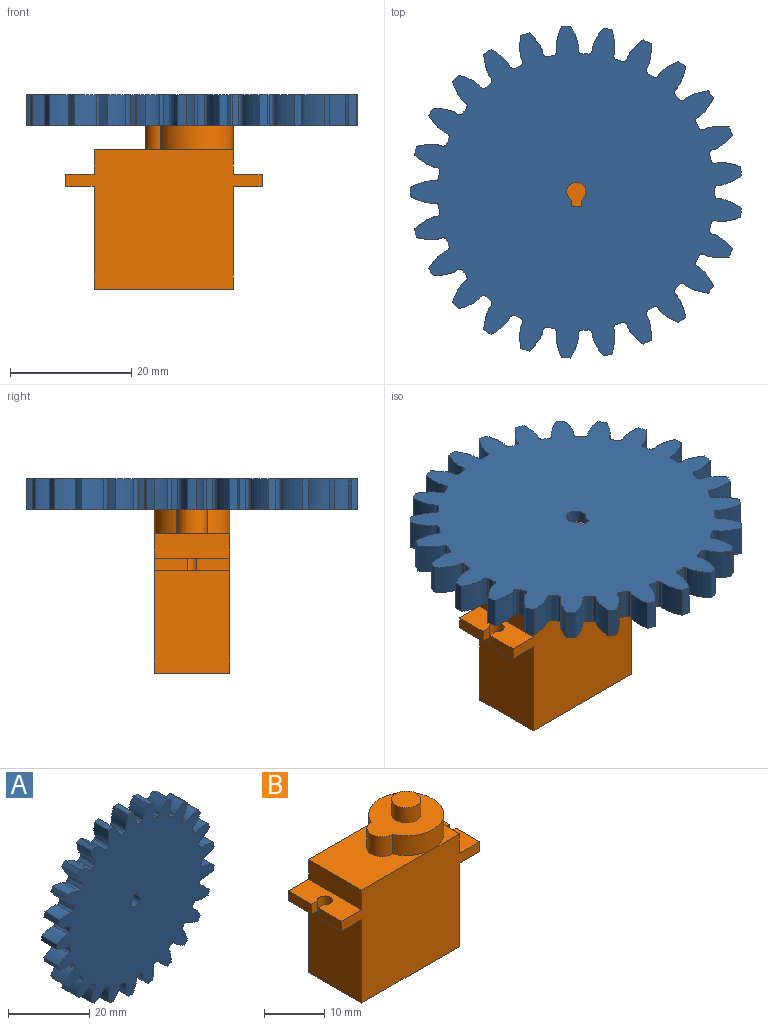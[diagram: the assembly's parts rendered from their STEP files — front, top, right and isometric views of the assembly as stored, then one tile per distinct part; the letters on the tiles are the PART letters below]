
ASSEMBLY  parts=2 mates=1
PART A: 156 faces, bbox 54.7x5.1x54.8 mm
  f0: cylinder r=27.43mm len=5.08mm, axis (0,1,0), area 7.4mm2, adj f24,f30,f141,f153
  f1: cylinder r=27.43mm len=5.08mm, axis (0,1,0), area 7.4mm2, adj f24,f30,f148,f151
  f2: cylinder r=27.43mm len=5.08mm, axis (0,1,0), area 7.4mm2, adj f24,f30,f136,f143
  f3: cylinder r=27.43mm len=5.08mm, axis (0,1,0), area 7.4mm2, adj f24,f30,f131,f138
  f4: cylinder r=27.43mm len=5.08mm, axis (0,1,0), area 7.4mm2, adj f24,f30,f126,f133
  f5: cylinder r=27.43mm len=5.08mm, axis (0,1,0), area 7.4mm2, adj f24,f30,f116,f128
  f6: cylinder r=27.43mm len=5.08mm, axis (0,1,0), area 7.4mm2, adj f24,f30,f111,f123
  f7: cylinder r=27.43mm len=5.08mm, axis (0,1,0), area 7.4mm2, adj f24,f30,f118,f121
  f8: cylinder r=27.43mm len=5.08mm, axis (0,1,0), area 7.4mm2, adj f24,f30,f106,f113
  f9: cylinder r=27.43mm len=5.08mm, axis (0,1,0), area 7.4mm2, adj f24,f30,f101,f108
  f10: cylinder r=27.43mm len=5.08mm, axis (0,1,0), area 7.4mm2, adj f24,f30,f96,f103
  f11: cylinder r=27.43mm len=5.08mm, axis (0,1,0), area 7.4mm2, adj f24,f30,f81,f98
  f12: cylinder r=27.43mm len=5.08mm, axis (0,1,0), area 7.4mm2, adj f24,f30,f31,f93
  f13: cylinder r=27.43mm len=5.08mm, axis (0,1,0), area 7.4mm2, adj f24,f30,f88,f91
  f14: cylinder r=27.43mm len=5.08mm, axis (0,1,0), area 7.4mm2, adj f24,f30,f76,f83
  f15: cylinder r=27.43mm len=5.08mm, axis (0,1,0), area 7.4mm2, adj f24,f30,f78,f86
  f16: cylinder r=27.43mm len=5.08mm, axis (0,1,0), area 7.4mm2, adj f24,f30,f73,f146
  f17: cylinder r=27.43mm len=5.08mm, axis (0,1,0), area 7.4mm2, adj f24,f30,f68,f71
  f18: cylinder r=27.43mm len=5.08mm, axis (0,1,0), area 7.4mm2, adj f24,f30,f63,f66
  f19: cylinder r=27.43mm len=5.08mm, axis (0,1,0), area 7.4mm2, adj f24,f30,f58,f61
  f20: cylinder r=27.43mm len=5.08mm, axis (0,1,0), area 7.4mm2, adj f24,f30,f46,f53
  f21: cylinder r=27.43mm len=5.08mm, axis (0,1,0), area 7.4mm2, adj f24,f30,f36,f48
  f22: cylinder r=27.43mm len=5.08mm, axis (0,1,0), area 7.4mm2, adj f24,f30,f43,f56
  f23: cylinder r=27.43mm len=5.08mm, axis (0,1,0), area 7.4mm2, adj f24,f30,f38,f41
  f24: plane 54.85x54.74mm, normal (0,-1,0), area 1985mm2, adj f0,f1,f2,f3,f4,f5,f6,f7
  f25: plane 5.08x1.01mm, normal (-1,0,0), area 5.1mm2, adj f24,f26,f28,f30
  f26: cylinder r=1.59mm len=5.08mm, axis (0,1,0), area 42.2mm2, adj f24,f25,f27,f30
  f27: plane 5.08x1.01mm, normal (1,0,0), area 5.1mm2, adj f24,f26,f28,f30
  f28: plane 5.08x1.59mm, normal (0,0,-1), area 8.1mm2, adj f24,f25,f27,f30
  f29: cylinder r=27.43mm len=5.08mm, axis (0,1,0), area 7.4mm2, adj f24,f30,f33,f51
  f30: plane 54.85x54.74mm, normal (0,1,0), area 1985mm2, adj f0,f1,f2,f3,f4,f5,f6,f7
  f31: extruded ~5.08x3.89mm, area 21.7mm2, adj f12,f24,f30,f34
  f32: cylinder r=22.86mm len=5.08mm, axis (0,1,0), area 5.4mm2, adj f24,f30,f34,f35
  f33: extruded ~5.08x3.89mm, area 21.7mm2, adj f24,f29,f30,f35
  f34: cylinder r=0.58mm len=5.08mm, axis (0,1,0), area 4.5mm2, adj f24,f30,f31,f32
  f35: cylinder r=0.58mm len=5.08mm, axis (0,1,0), area 4.5mm2, adj f24,f30,f32,f33
  f36: extruded ~5.08x3.93mm, area 21.7mm2, adj f21,f24,f30,f39
  f37: cylinder r=22.86mm len=5.08mm, axis (0,1,0), area 5.4mm2, adj f24,f30,f39,f40
  f38: extruded ~5.08x3.83mm, area 21.7mm2, adj f23,f24,f30,f40
  f39: cylinder r=0.58mm len=5.08mm, axis (0,1,0), area 4.5mm2, adj f24,f30,f36,f37
  f40: cylinder r=0.58mm len=5.08mm, axis (0,1,0), area 4.5mm2, adj f24,f30,f37,f38
  f41: extruded ~5.08x3.43mm, area 21.7mm2, adj f23,f24,f30,f44
  f42: cylinder r=22.86mm len=5.08mm, axis (0,1,0), area 5.4mm2, adj f24,f30,f44,f45
  f43: extruded ~5.08x4.14mm, area 21.7mm2, adj f22,f24,f30,f45
  f44: cylinder r=0.58mm len=5.08mm, axis (0,1,0), area 4.5mm2, adj f24,f30,f41,f42
  f45: cylinder r=0.58mm len=5.08mm, axis (0,1,0), area 4.5mm2, adj f24,f30,f42,f43
  f46: extruded ~5.08x4.18mm, area 21.7mm2, adj f20,f24,f30,f49
  f47: cylinder r=22.86mm len=5.08mm, axis (0,1,0), area 5.4mm2, adj f24,f30,f49,f50
  f48: extruded ~5.08x3.27mm, area 21.7mm2, adj f21,f24,f30,f50
  f49: cylinder r=0.58mm len=5.08mm, axis (0,1,0), area 4.5mm2, adj f24,f30,f46,f47
  f50: cylinder r=0.58mm len=5.08mm, axis (0,1,0), area 4.5mm2, adj f24,f30,f47,f48
  f51: extruded ~5.08x4.17mm, area 21.7mm2, adj f24,f29,f30,f54
  f52: cylinder r=22.86mm len=5.08mm, axis (0,1,0), area 5.4mm2, adj f24,f30,f54,f55
  f53: extruded ~5.08x3.38mm, area 21.7mm2, adj f20,f24,f30,f55
  f54: cylinder r=0.58mm len=5.08mm, axis (0,1,0), area 4.5mm2, adj f24,f30,f51,f52
  f55: cylinder r=0.58mm len=5.08mm, axis (0,1,0), area 4.5mm2, adj f24,f30,f52,f53
  f56: extruded ~5.08x3.21mm, area 21.7mm2, adj f22,f24,f30,f59
  f57: cylinder r=22.86mm len=5.08mm, axis (0,1,0), area 5.4mm2, adj f24,f30,f59,f60
  f58: extruded ~5.08x4.2mm, area 21.7mm2, adj f19,f24,f30,f60
  f59: cylinder r=0.58mm len=5.08mm, axis (0,1,0), area 4.5mm2, adj f24,f30,f56,f57
  f60: cylinder r=0.58mm len=5.08mm, axis (0,1,0), area 4.5mm2, adj f24,f30,f57,f58
  f61: extruded ~5.08x3.79mm, area 21.7mm2, adj f19,f24,f30,f64
  f62: cylinder r=22.86mm len=5.08mm, axis (0,1,0), area 5.4mm2, adj f24,f30,f64,f65
  f63: extruded ~5.08x3.99mm, area 21.7mm2, adj f18,f24,f30,f65
  f64: cylinder r=0.58mm len=5.08mm, axis (0,1,0), area 4.5mm2, adj f24,f30,f61,f62
  f65: cylinder r=0.58mm len=5.08mm, axis (0,1,0), area 4.5mm2, adj f24,f30,f62,f63
  f66: extruded ~5.08x4.12mm, area 21.7mm2, adj f18,f24,f30,f69
  f67: cylinder r=22.86mm len=5.08mm, axis (0,1,0), area 5.4mm2, adj f24,f30,f69,f70
  f68: extruded ~5.08x3.53mm, area 21.7mm2, adj f17,f24,f30,f70
  f69: cylinder r=0.58mm len=5.08mm, axis (0,1,0), area 4.5mm2, adj f24,f30,f66,f67
  f70: cylinder r=0.58mm len=5.08mm, axis (0,1,0), area 4.5mm2, adj f24,f30,f67,f68
  f71: extruded ~5.08x4.2mm, area 21.7mm2, adj f17,f24,f30,f74
  f72: cylinder r=22.86mm len=5.08mm, axis (0,1,0), area 5.4mm2, adj f24,f30,f74,f75
  f73: extruded ~5.08x3.1mm, area 21.7mm2, adj f16,f24,f30,f75
  f74: cylinder r=0.58mm len=5.08mm, axis (0,1,0), area 4.5mm2, adj f24,f30,f71,f72
  f75: cylinder r=0.58mm len=5.08mm, axis (0,1,0), area 4.5mm2, adj f24,f30,f72,f73
  f76: extruded ~5.08x3.83mm, area 21.7mm2, adj f14,f24,f30,f79
  f77: cylinder r=22.86mm len=5.08mm, axis (0,1,0), area 5.4mm2, adj f24,f30,f79,f80
  f78: extruded ~5.08x3.93mm, area 21.7mm2, adj f15,f24,f30,f80
  f79: cylinder r=0.58mm len=5.08mm, axis (0,1,0), area 4.5mm2, adj f24,f30,f76,f77
  f80: cylinder r=0.58mm len=5.08mm, axis (0,1,0), area 4.5mm2, adj f24,f30,f77,f78
  f81: extruded ~5.08x4.14mm, area 21.7mm2, adj f11,f24,f30,f84
  f82: cylinder r=22.86mm len=5.08mm, axis (0,1,0), area 5.4mm2, adj f24,f30,f84,f85
  f83: extruded ~5.08x3.43mm, area 21.7mm2, adj f14,f24,f30,f85
  f84: cylinder r=0.58mm len=5.08mm, axis (0,1,0), area 4.5mm2, adj f24,f30,f81,f82
  f85: cylinder r=0.58mm len=5.08mm, axis (0,1,0), area 4.5mm2, adj f24,f30,f82,f83
  f86: extruded ~5.08x3.27mm, area 21.7mm2, adj f15,f24,f30,f89
  f87: cylinder r=22.86mm len=5.08mm, axis (0,1,0), area 5.4mm2, adj f24,f30,f89,f90
  f88: extruded ~5.08x4.18mm, area 21.7mm2, adj f13,f24,f30,f90
  f89: cylinder r=0.58mm len=5.08mm, axis (0,1,0), area 4.5mm2, adj f24,f30,f86,f87
  f90: cylinder r=0.58mm len=5.08mm, axis (0,1,0), area 4.5mm2, adj f24,f30,f87,f88
  f91: extruded ~5.08x3.38mm, area 21.7mm2, adj f13,f24,f30,f94
  f92: cylinder r=22.86mm len=5.08mm, axis (0,1,0), area 5.4mm2, adj f24,f30,f94,f95
  f93: extruded ~5.08x4.17mm, area 21.7mm2, adj f12,f24,f30,f95
  f94: cylinder r=0.58mm len=5.08mm, axis (0,1,0), area 4.5mm2, adj f24,f30,f91,f92
  f95: cylinder r=0.58mm len=5.08mm, axis (0,1,0), area 4.5mm2, adj f24,f30,f92,f93
  f96: extruded ~5.08x4.2mm, area 21.7mm2, adj f10,f24,f30,f99
  f97: cylinder r=22.86mm len=5.08mm, axis (0,1,0), area 5.4mm2, adj f24,f30,f99,f100
  f98: extruded ~5.08x3.21mm, area 21.7mm2, adj f11,f24,f30,f100
  f99: cylinder r=0.58mm len=5.08mm, axis (0,1,0), area 4.5mm2, adj f24,f30,f96,f97
  f100: cylinder r=0.58mm len=5.08mm, axis (0,1,0), area 4.5mm2, adj f24,f30,f97,f98
  f101: extruded ~5.08x3.99mm, area 21.7mm2, adj f9,f24,f30,f104
  f102: cylinder r=22.86mm len=5.08mm, axis (0,1,0), area 5.4mm2, adj f24,f30,f104,f105
  f103: extruded ~5.08x3.79mm, area 21.7mm2, adj f10,f24,f30,f105
  f104: cylinder r=0.58mm len=5.08mm, axis (0,1,0), area 4.5mm2, adj f24,f30,f101,f102
  f105: cylinder r=0.58mm len=5.08mm, axis (0,1,0), area 4.5mm2, adj f24,f30,f102,f103
  f106: extruded ~5.08x3.53mm, area 21.7mm2, adj f8,f24,f30,f109
  f107: cylinder r=22.86mm len=5.08mm, axis (0,1,0), area 5.4mm2, adj f24,f30,f109,f110
  f108: extruded ~5.08x4.12mm, area 21.7mm2, adj f9,f24,f30,f110
  f109: cylinder r=0.58mm len=5.08mm, axis (0,1,0), area 4.5mm2, adj f24,f30,f106,f107
  f110: cylinder r=0.58mm len=5.08mm, axis (0,1,0), area 4.5mm2, adj f24,f30,f107,f108
  f111: extruded ~5.08x3.1mm, area 21.7mm2, adj f6,f24,f30,f114
  f112: cylinder r=22.86mm len=5.08mm, axis (0,1,0), area 5.4mm2, adj f24,f30,f114,f115
  f113: extruded ~5.08x4.2mm, area 21.7mm2, adj f8,f24,f30,f115
  f114: cylinder r=0.58mm len=5.08mm, axis (0,1,0), area 4.5mm2, adj f24,f30,f111,f112
  f115: cylinder r=0.58mm len=5.08mm, axis (0,1,0), area 4.5mm2, adj f24,f30,f112,f113
  f116: extruded ~5.08x4.09mm, area 21.7mm2, adj f5,f24,f30,f119
  f117: cylinder r=22.86mm len=5.08mm, axis (0,1,0), area 5.4mm2, adj f24,f30,f119,f120
  f118: extruded ~5.08x3.58mm, area 21.7mm2, adj f7,f24,f30,f120
  f119: cylinder r=0.58mm len=5.08mm, axis (0,1,0), area 4.5mm2, adj f24,f30,f116,f117
  f120: cylinder r=0.58mm len=5.08mm, axis (0,1,0), area 4.5mm2, adj f24,f30,f117,f118
  f121: extruded ~5.08x3.71mm, area 21.7mm2, adj f7,f24,f30,f124
  f122: cylinder r=22.86mm len=5.08mm, axis (0,1,0), area 5.4mm2, adj f24,f30,f124,f125
  f123: extruded ~5.08x4.02mm, area 21.7mm2, adj f6,f24,f30,f125
  f124: cylinder r=0.58mm len=5.08mm, axis (0,1,0), area 4.5mm2, adj f24,f30,f121,f122
  f125: cylinder r=0.58mm len=5.08mm, axis (0,1,0), area 4.5mm2, adj f24,f30,f122,f123
  f126: extruded ~5.08x4.21mm, area 21.7mm2, adj f4,f24,f30,f129
  f127: cylinder r=22.86mm len=5.08mm, axis (0,1,0), area 5.4mm2, adj f24,f30,f129,f130
  f128: extruded ~5.08x3.03mm, area 21.7mm2, adj f5,f24,f30,f130
  f129: cylinder r=0.58mm len=5.08mm, axis (0,1,0), area 4.5mm2, adj f24,f30,f126,f127
  f130: cylinder r=0.58mm len=5.08mm, axis (0,1,0), area 4.5mm2, adj f24,f30,f127,f128
  f131: extruded ~5.08x4.06mm, area 21.7mm2, adj f3,f24,f30,f134
  f132: cylinder r=22.86mm len=5.08mm, axis (0,1,0), area 5.4mm2, adj f24,f30,f134,f135
  f133: extruded ~5.08x3.66mm, area 21.7mm2, adj f4,f24,f30,f135
  f134: cylinder r=0.58mm len=5.08mm, axis (0,1,0), area 4.5mm2, adj f24,f30,f131,f132
  f135: cylinder r=0.58mm len=5.08mm, axis (0,1,0), area 4.5mm2, adj f24,f30,f132,f133
  f136: extruded ~5.08x3.66mm, area 21.7mm2, adj f2,f24,f30,f139
  f137: cylinder r=22.86mm len=5.08mm, axis (0,1,0), area 5.4mm2, adj f24,f30,f139,f140
  f138: extruded ~5.08x4.06mm, area 21.7mm2, adj f3,f24,f30,f140
  f139: cylinder r=0.58mm len=5.08mm, axis (0,1,0), area 4.5mm2, adj f24,f30,f136,f137
  f140: cylinder r=0.58mm len=5.08mm, axis (0,1,0), area 4.5mm2, adj f24,f30,f137,f138
  f141: extruded ~5.08x3.03mm, area 21.7mm2, adj f0,f24,f30,f144
  f142: cylinder r=22.86mm len=5.08mm, axis (0,1,0), area 5.4mm2, adj f24,f30,f144,f145
  f143: extruded ~5.08x4.21mm, area 21.7mm2, adj f2,f24,f30,f145
  f144: cylinder r=0.58mm len=5.08mm, axis (0,1,0), area 4.5mm2, adj f24,f30,f141,f142
  f145: cylinder r=0.58mm len=5.08mm, axis (0,1,0), area 4.5mm2, adj f24,f30,f142,f143
  f146: extruded ~5.08x4.02mm, area 21.7mm2, adj f16,f24,f30,f149
  f147: cylinder r=22.86mm len=5.08mm, axis (0,1,0), area 5.4mm2, adj f24,f30,f149,f150
  f148: extruded ~5.08x3.71mm, area 21.7mm2, adj f1,f24,f30,f150
  f149: cylinder r=0.58mm len=5.08mm, axis (0,1,0), area 4.5mm2, adj f24,f30,f146,f147
  f150: cylinder r=0.58mm len=5.08mm, axis (0,1,0), area 4.5mm2, adj f24,f30,f147,f148
  f151: extruded ~5.08x3.58mm, area 21.7mm2, adj f1,f24,f30,f154
  f152: cylinder r=22.86mm len=5.08mm, axis (0,1,0), area 5.4mm2, adj f24,f30,f154,f155
  f153: extruded ~5.08x4.09mm, area 21.7mm2, adj f0,f24,f30,f155
  f154: cylinder r=0.58mm len=5.08mm, axis (0,1,0), area 4.5mm2, adj f24,f30,f151,f152
  f155: cylinder r=0.58mm len=5.08mm, axis (0,1,0), area 4.5mm2, adj f24,f30,f152,f153
PART B: 29 faces, bbox 32.5x12.6x30 mm
  f0: plane 4.99x4.9mm, normal (0,0,1), area 18.9mm2, adj f1
  f1: cylinder r=2.45mm len=4.9mm, axis (0,0,1), area 46.2mm2, adj f0,f2
  f2: plane 14.61x12.65mm, normal (0,0,1), area 112mm2, adj f1,f3,f4
  f3: cylinder r=2.5mm len=5mm, axis (0,0,1), area 31.6mm2, adj f2,f4,f10
  f4: cylinder r=6.25mm len=12.5mm, axis (0,0,1), area 136.5mm2, adj f2,f3,f8,f10,f11
  f5: plane 2x1.38mm, normal (0,-1,0), area 2.7mm2, adj f6,f9,f13,f15
  f6: cylinder r=1.25mm len=2.5mm, axis (0,0,-1), area 12.5mm2, adj f5,f7,f13,f15
  f7: plane 2x1.38mm, normal (0,1,0), area 2.7mm2, adj f6,f13,f14,f15
  f8: plane 6.25x6.25mm, normal (0,0,1), area 8.4mm2, adj f4,f12,f20
  f9: plane 5.5x2mm, normal (1,0,0), area 11mm2, adj f5,f13,f15,f20
  f10: plane 16.75x12.5mm, normal (0,0,1), area 139.8mm2, adj f3,f4,f18,f20,f22
  f11: plane 6.25x6.25mm, normal (0,0,1), area 8.4mm2, adj f4,f12,f22
  f12: plane 12.5x4mm, normal (1,0,0), area 50mm2, adj f8,f11,f13,f20,f22
  f13: plane 12.5x4.75mm, normal (0,0,1), area 52.7mm2, adj f5,f6,f7,f9,f12,f14,f20,f22
  f14: plane 5.5x2mm, normal (1,0,0), area 11mm2, adj f7,f13,f15,f22
  f15: plane 12.5x4.75mm, normal (0,0,-1), area 52.7mm2, adj f5,f6,f7,f9,f14,f16,f20,f22
  f16: plane 17x12.5mm, normal (1,0,0), area 212.5mm2, adj f15,f17,f20,f22
  f17: plane 23x12.5mm, normal (0,0,-1), area 287.5mm2, adj f16,f20,f21,f22
  f18: plane 12.5x4mm, normal (-1,0,0), area 50mm2, adj f10,f20,f22,f25
  f19: plane 5.5x2mm, normal (-1,0,0), area 11mm2, adj f20,f24,f25,f27
  f20: plane 32.5x23mm, normal (0,1,0), area 548mm2, adj f8,f9,f10,f12,f13,f15,f16,f17
  f21: plane 17x12.5mm, normal (-1,0,0), area 212.5mm2, adj f17,f20,f22,f27
  f22: plane 32.5x23mm, normal (0,-1,0), area 548mm2, adj f10,f11,f12,f13,f14,f15,f16,f17
  f23: plane 5.5x2mm, normal (-1,0,0), area 11mm2, adj f22,f25,f26,f27
  f24: plane 2x1.38mm, normal (0,-1,0), area 2.8mm2, adj f19,f25,f27,f28
  f25: plane 12.5x4.75mm, normal (0,0,1), area 52.7mm2, adj f18,f19,f20,f22,f23,f24,f26,f28
  f26: plane 2x1.38mm, normal (0,1,0), area 2.8mm2, adj f23,f25,f27,f28
  f27: plane 12.5x4.75mm, normal (0,0,-1), area 52.7mm2, adj f19,f20,f21,f22,f23,f24,f26,f28
  f28: cylinder r=1.25mm len=2.5mm, axis (0,0,-1), area 12.5mm2, adj f24,f25,f26,f27
PLACE A rot(axis=(1,0,0),90deg) t=(-4.18,9.36,38.31)mm
PLACE B t=(2.58,3.11,6.23)mm
MATE fastened A.f0 <-> B.f2  axis (0,0,-1) through (-4.18,9.36,33.23)mm
